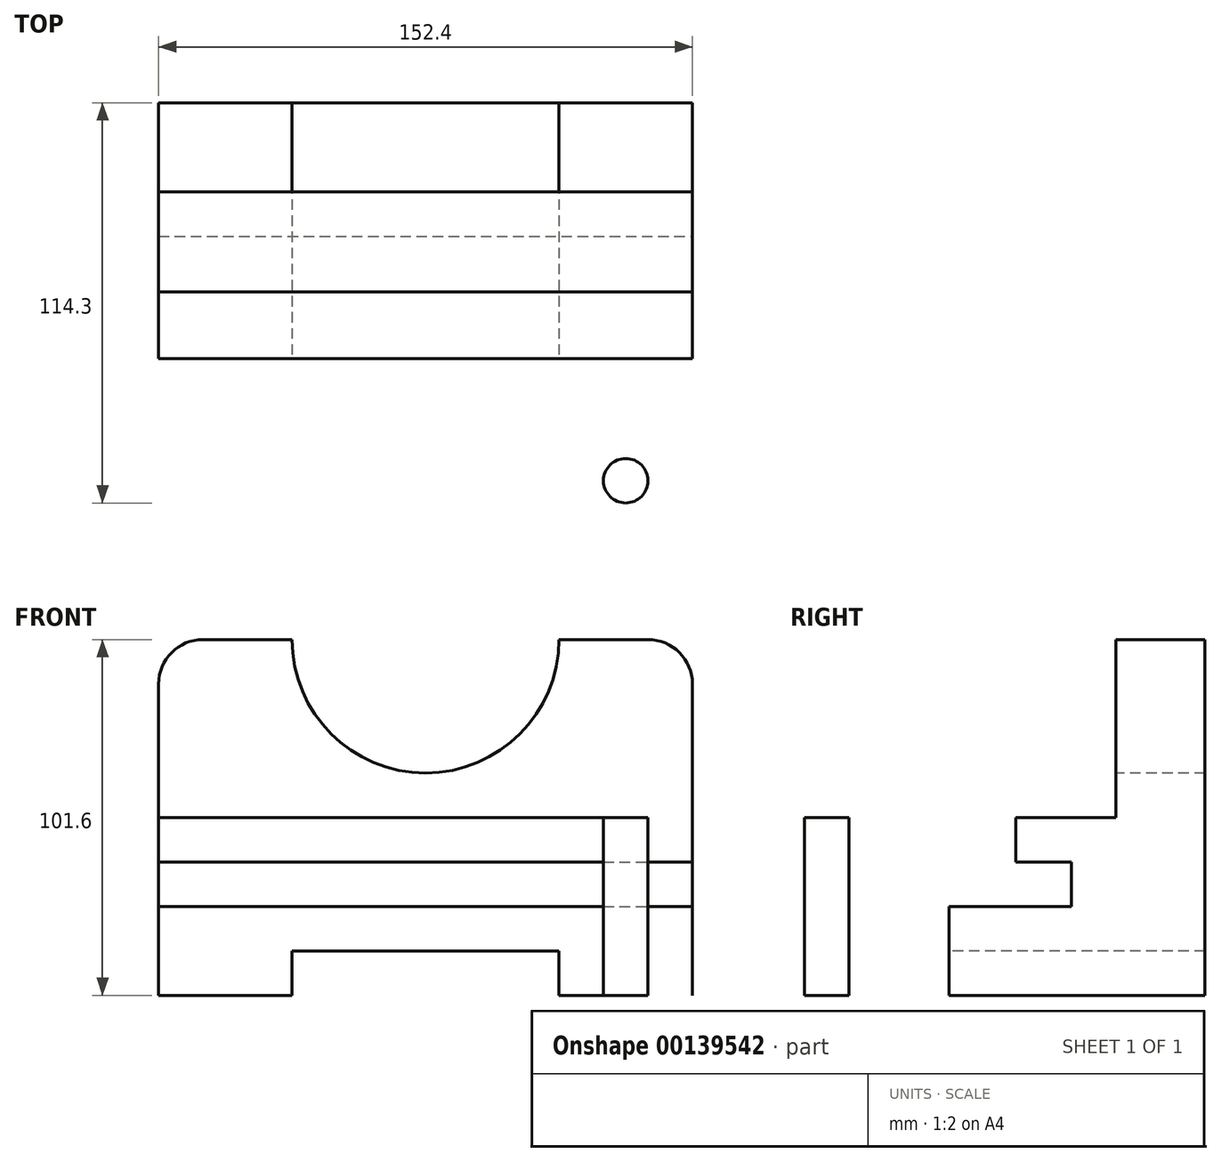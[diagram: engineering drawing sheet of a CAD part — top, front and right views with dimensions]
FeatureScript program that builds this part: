
annotation { "Feature Type Name" : "Feature", "Feature Type Description" : "" }
export const myFeature = defineFeature(function(context is Context, id is Id, definition is map)
    precondition{}
    {
        {
            var Q0;
            Q0=qCreatedBy(makeId("Right.planeOp"),FACE);
            var sketch = newSketch(context, id + "F0", { "sketchPlane" : qUnion([Q0])});
            skLineSegment(sketch, "E0", {"start": v(0, 0) * mm, "end": v(0, 50.8) * mm});
            skLineSegment(sketch, "E1", {"start": v(0, 50.8) * mm, "end": v(53.97, 50.8) * mm});
            skLineSegment(sketch, "E2", {"start": v(53.97, 50.8) * mm, "end": v(53.97, 38.1) * mm});
            skLineSegment(sketch, "E3", {"start": v(0, 0) * mm, "end": v(127, 0) * mm});
            skLineSegment(sketch, "E4", {"start": v(127, 0) * mm, "end": v(127, 101.6) * mm});
            skLineSegment(sketch, "E5", {"start": v(127, 101.6) * mm, "end": v(101.6, 101.6) * mm});
            skLineSegment(sketch, "E6", {"start": v(101.6, 101.6) * mm, "end": v(101.6, 50.8) * mm});
            skLineSegment(sketch, "E7", {"start": v(101.6, 50.8) * mm, "end": v(73.03, 50.8) * mm});
            skLineSegment(sketch, "E8", {"start": v(73.03, 50.8) * mm, "end": v(73.03, 38.1) * mm});
            skLineSegment(sketch, "E9", {"start": v(73.03, 38.1) * mm, "end": v(88.9, 38.1) * mm});
            skLineSegment(sketch, "E10", {"start": v(88.9, 38.1) * mm, "end": v(88.9, 25.4) * mm});
            skLineSegment(sketch, "E11", {"start": v(88.9, 25.4) * mm, "end": v(38.1, 25.4) * mm});
            skLineSegment(sketch, "E12", {"start": v(38.1, 25.4) * mm, "end": v(38.1, 38.1) * mm});
            skLineSegment(sketch, "E13", {"start": v(38.1, 38.1) * mm, "end": v(53.97, 38.1) * mm});
            skSolve(sketch);
        }
        {
            var Q0;
            Q0 = qSketchRegion(id + "F0", true);
            extrude(context, id + "F1", {"entities" : qUnion([Q0]), "oppositeDirection" : true, "depth" : 152.4 * mm});
        }
        {
            var Q0;
            Q0=makeQuery(id+"F1.opExtrude","SWEPT_FACE",FACE,{"disambiguationData":[OSD([sQuery(id+"F0.wireOp",EDGE,"E0")])]});
            var sketch = newSketch(context, id + "F2", { "sketchPlane" : qUnion([Q0])});
            skLineSegment(sketch, "E14.0", {"start": v(-152.4, 0) * mm, "end": v(0, 0) * mm});
            skLineSegment(sketch, "E15", {"start": v(-76.2, 0) * mm, "end": v(-76.2, 12.7) * mm, "construction": true});
            skLineSegment(sketch, "E16", {"start": v(-114.3, 12.7) * mm, "end": v(-38.1, 12.7) * mm});
            skLineSegment(sketch, "E17", {"start": v(-114.3, 12.7) * mm, "end": v(-114.3, 0) * mm});
            skLineSegment(sketch, "E18", {"start": v(-38.1, 12.7) * mm, "end": v(-38.1, 0) * mm});
            skSolve(sketch);
        }
        {
            var Q0;
            Q0 = qSketchRegion(id + "F2", true);
            extrude(context, id + "F3", {"entities" : qUnion([Q0]), "operationType" : NewBodyOperationType.REMOVE, "endBound" : BoundingType.THROUGH_ALL, "oppositeDirection" : true, "depth" : 25.4 * mm});
        }
        {
            var Q0;
            Q0=makeQuery(id+"F1.opExtrude","SWEPT_FACE",FACE,{"disambiguationData":[OSD([sQuery(id+"F0.wireOp",EDGE,"E6")])]});
            var sketch = newSketch(context, id + "F4", { "sketchPlane" : qUnion([Q0])});
            skLineSegment(sketch, "E19.0", {"start": v(-152.4, 101.6) * mm, "end": v(0, 101.6) * mm});
            skArc(sketch, "E20", {"start": v(-114.3, 101.6) * mm, "mid": v(-76.2, 63.5) * mm, "end": v(-38.1, 101.6) * mm});
            skSolve(sketch);
        }
        {
            var Q0;
            Q0 = qSketchRegion(id + "F4", true);
            var Q1;
            Q1=makeQuery(id+"F1.opExtrude","SWEPT_FACE",FACE,{"disambiguationData":[OSD([sQuery(id+"F0.wireOp",EDGE,"E4")])]});
            extrude(context, id + "F5", {"entities" : qUnion([Q0]), "operationType" : NewBodyOperationType.REMOVE, "endBound" : BoundingType.UP_TO_SURFACE, "oppositeDirection" : true, "endBoundEntityFace" : qUnion([Q1]), "depth" : 25.4 * mm});
        }
        {
            var Q0;
            Q0=makeQuery(id+"F1.opExtrude","CAP_EDGE",EDGE,{"disambiguationData":[OSD([sQuery(id+"F0.wireOp",EDGE,"E5")])],"isStart":true});
            var Q1;
            Q1=makeQuery(id+"F1.opExtrude","CAP_EDGE",EDGE,{"disambiguationData":[OSD([sQuery(id+"F0.wireOp",EDGE,"E5")])],"isStart":false});
            fillet(context, id + "F6", {"entities" : qUnion([Q0, Q1]), "radius" : 12.7 * mm, "tangentPropagation" : true, "allowEdgeOverflow" : false});
        }
        {
            var Q0;
            Q0=makeQuery(id+"F1.opExtrude","SWEPT_FACE",FACE,{"disambiguationData":[OSD([sQuery(id+"F0.wireOp",EDGE,"E1")])]});
            var sketch = newSketch(context, id + "F7", { "sketchPlane" : qUnion([Q0])});
            skLineSegment(sketch, "E21.0", {"start": v(-152.4, 0) * mm, "end": v(0, 0) * mm, "construction": true});
            skLineSegment(sketch, "E22.0", {"start": v(-152.4, 53.97) * mm, "end": v(0, 53.97) * mm, "construction": true});
            skLineSegment(sketch, "E23.0", {"start": v(-152.4, 0) * mm, "end": v(-152.4, 53.97) * mm, "construction": true});
            skLineSegment(sketch, "E24.0", {"start": v(0, 0) * mm, "end": v(0, 53.97) * mm, "construction": true});
            skPoint(sketch, "E25", {"position": v(-133.35, 19.05) * mm});
            skCircle(sketch, "E26", {"center": v(-133.35, 19.05) * mm, "radius": 6.35 * mm});
            skLineSegment(sketch, "E27", {"start": v(-76.2, 53.97) * mm, "end": v(-76.2, 0) * mm, "construction": true});
            skCircle(sketch, "E28.MirrorC", {"center": v(-19.05, 19.05) * mm, "radius": 6.35 * mm});
            skSolve(sketch);
        }
        {
            var Q0;
            Q0=makeQuery(id+"F7.imprint","IMPRINT",FACE,{"disambiguationData":[TD([[makeQuery(id+"F7.imprint","IMPRINT",EDGE,{"derivedFrom":sQuery(id+"F7.wireOp",EDGE,"E26")}),1.0]])]});
            var Q1;
            Q1=makeQuery(id+"F7.imprint","IMPRINT",FACE,{"disambiguationData":[TD([[makeQuery(id+"F7.imprint","IMPRINT",EDGE,{"derivedFrom":sQuery(id+"F7.wireOp",EDGE,"E28.MirrorC")}),-1.0]])]});
            extrude(context, id + "F8", {"entities" : qUnion([Q0, Q1]), "operationType" : NewBodyOperationType.REMOVE, "endBound" : BoundingType.THROUGH_ALL, "oppositeDirection" : true, "depth" : 25.4 * mm});
        }
    });
